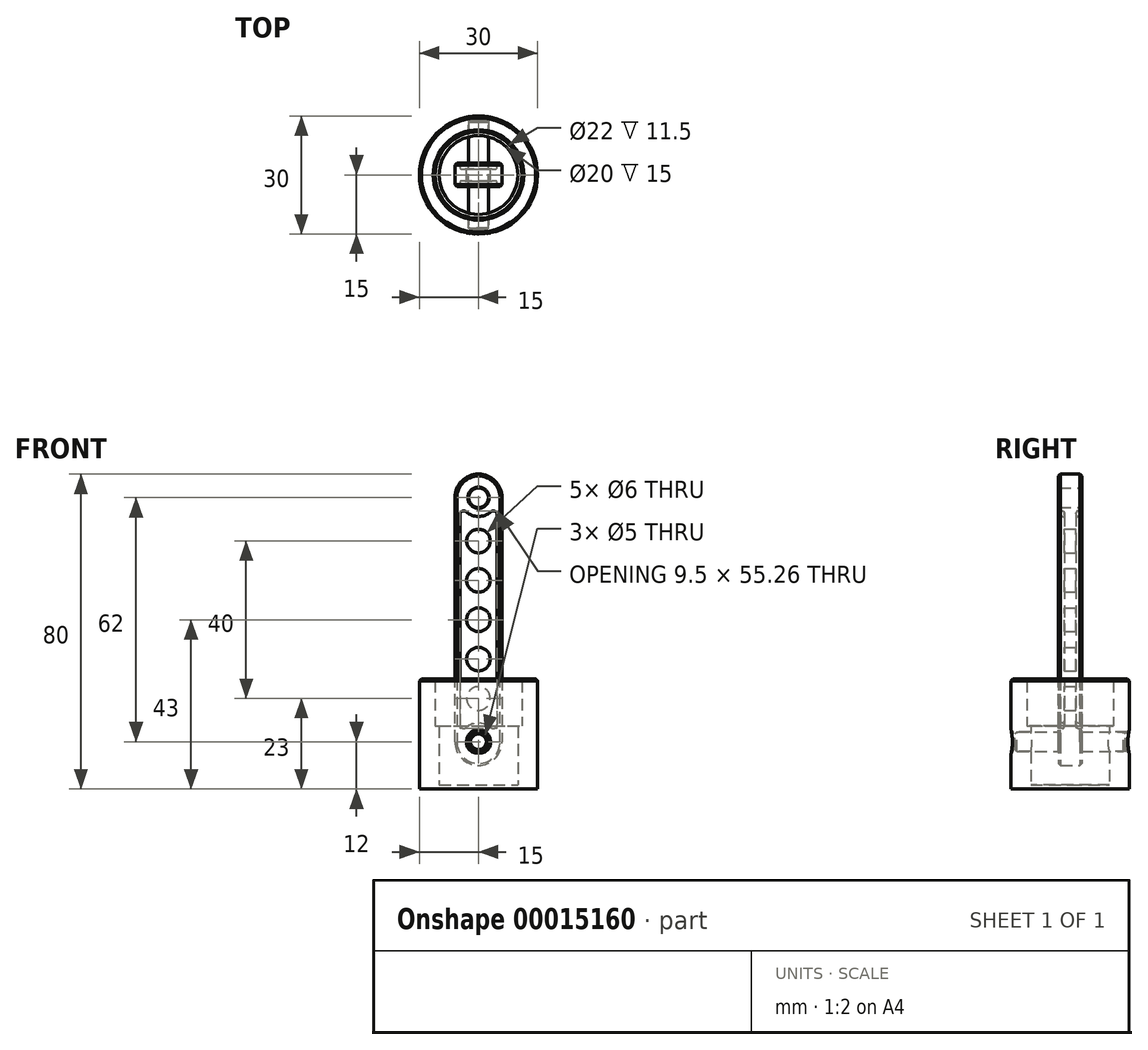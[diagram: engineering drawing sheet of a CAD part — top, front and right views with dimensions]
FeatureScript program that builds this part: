
annotation { "Feature Type Name" : "Feature", "Feature Type Description" : "" }
export const myFeature = defineFeature(function(context is Context, id is Id, definition is map)
    precondition{}
    {
        {
            var Q0;
            Q0=qCreatedBy(makeId("Front.planeOp"),FACE);
            var sketch = newSketch(context, id + "F0", { "sketchPlane" : qUnion([Q0])});
            skLineSegment(sketch, "E0", {"start": v(0, 0) * mm, "end": v(15, 0) * mm});
            skLineSegment(sketch, "E1", {"start": v(15, 0) * mm, "end": v(15, 28) * mm});
            skLineSegment(sketch, "E2", {"start": v(15, 28) * mm, "end": v(11, 28) * mm});
            skLineSegment(sketch, "E3", {"start": v(11, 28) * mm, "end": v(11, 16) * mm});
            skLineSegment(sketch, "E4", {"start": v(11, 16) * mm, "end": v(10, 16) * mm});
            skLineSegment(sketch, "E5", {"start": v(10, 16) * mm, "end": v(10, 1) * mm});
            skLineSegment(sketch, "E6", {"start": v(10, 1) * mm, "end": v(0, 1) * mm});
            skLineSegment(sketch, "E7", {"start": v(0, 1) * mm, "end": v(0, 0) * mm});
            skLineSegment(sketch, "E8", {"start": v(0, 0) * mm, "end": v(0, 33.28) * mm, "construction": true});
            skCircle(sketch, "E9", {"center": v(0, 12) * mm, "radius": 2.5 * mm});
            skSolve(sketch);
        }
        {
            var Q0;
            Q0=makeQuery(id+"F0.imprint","IMPRINT",FACE,{"disambiguationData":[TD([[makeQuery(id+"F0.imprint","IMPRINT",EDGE,{"derivedFrom":sQuery(id+"F0.wireOp",EDGE,"E0")}),1.0]])]});
            var Q1;
            Q1=sQuery(id+"F0.wireOp",EDGE,"E8");
            revolve(context, id + "F1", {"entities" : qUnion([Q0]), "axis" : qUnion([Q1]), "revolveType" : RevolveType.FULL});
        }
        {
            var Q0;
            Q0=makeQuery(id+"F0.imprint","IMPRINT",FACE,{"disambiguationData":[TD([[makeQuery(id+"F0.imprint","IMPRINT",EDGE,{"derivedFrom":sQuery(id+"F0.wireOp",EDGE,"E9")}),1.0]])]});
            extrude(context, id + "F2", {"entities" : qUnion([Q0]), "operationType" : NewBodyOperationType.REMOVE, "endBound" : BoundingType.THROUGH_ALL, "oppositeDirection" : true, "depth" : 44.36 * mm, "hasSecondDirection" : true, "secondDirectionBound" : SecondDirectionBoundingType.THROUGH_ALL, "secondDirectionOppositeDirection" : false, "secondDirectionDepth" : 25 * mm});
        }
        {
            var Q0;
            Q0=makeQuery(id+"F1.opRevolve","SWEPT_EDGE",EDGE,{"disambiguationData":[OSD([sQuery(id+"F0.wireOp",EDGE,"E1"),sQuery(id+"F0.wireOp",EDGE,"E2")])]});
            var Q1;
            Q1=makeQuery(id+"F1.opRevolve","SWEPT_EDGE",EDGE,{"disambiguationData":[OSD([sQuery(id+"F0.wireOp",EDGE,"E2"),sQuery(id+"F0.wireOp",EDGE,"E3")])]});
            chamfer(context, id + "F3", {"entities" : qUnion([Q0, Q1]), "width" : .5 * mm, "tangentPropagation" : true});
        }
        {
            var Q0;
            Q0=makeQuery(id+"F2.boolean.opBoolean","INTERSECT",EDGE,{"disambiguationData":[OD(0.0)],"derivedFrom":[makeQuery(id+"F1.opRevolve","SWEPT_FACE",FACE,{"disambiguationData":[OSD([sQuery(id+"F0.wireOp",EDGE,"E1")])]}),makeQuery(id+"F2.opExtrude","SWEPT_FACE",FACE,{"disambiguationData":[OSD([sQuery(id+"F0.wireOp",EDGE,"E9")])]})]});
            var Q1;
            Q1=makeQuery(id+"F2.boolean.opBoolean","INTERSECT",EDGE,{"disambiguationData":[OD(1.0)],"derivedFrom":[makeQuery(id+"F1.opRevolve","SWEPT_FACE",FACE,{"disambiguationData":[OSD([sQuery(id+"F0.wireOp",EDGE,"E1")])]}),makeQuery(id+"F2.opExtrude","SWEPT_FACE",FACE,{"disambiguationData":[OSD([sQuery(id+"F0.wireOp",EDGE,"E9")])]})]});
            chamfer(context, id + "F4", {"entities" : qUnion([Q0, Q1]), "width" : .5 * mm, "tangentPropagation" : true});
        }
        {
            var Q0;
            Q0=makeQuery(id+"F0.imprint","IMPRINT",FACE,{"disambiguationData":[TD([[makeQuery(id+"F0.imprint","IMPRINT",EDGE,{"derivedFrom":sQuery(id+"F0.wireOp",EDGE,"E9")}),1.0]])]});
            var Q1;
            Q1=sQuery(id+"F0.wireOp",EDGE,"E9");
            extrude(context, id + "F5", {"entities" : qUnion([Q0]), "surfaceEntities" : qUnion([Q1]), "endBound" : BoundingType.SYMMETRIC, "depth" : 28 * mm});
        }
        {
            var Q0;
            Q0=makeQuery(id+"F5.opExtrude","CAP_EDGE",EDGE,{"disambiguationData":[OSD([sQuery(id+"F0.wireOp",EDGE,"E9")])],"isStart":true});
            var Q1;
            Q1=makeQuery(id+"F5.opExtrude","CAP_EDGE",EDGE,{"disambiguationData":[OSD([sQuery(id+"F0.wireOp",EDGE,"E9")])],"isStart":false});
            chamfer(context, id + "F6", {"entities" : qUnion([Q0, Q1]), "width" : .5 * mm, "tangentPropagation" : true});
        }
        {
            var Q0;
            Q0=qCreatedBy(makeId("Front.planeOp"),FACE);
            var sketch = newSketch(context, id + "F7", { "sketchPlane" : qUnion([Q0])});
            skCircle(sketch, "E10.0", {"center": v(0, 12) * mm, "radius": 2.5 * mm});
            skLineSegment(sketch, "E11", {"start": v(0, 12) * mm, "end": v(0, 74) * mm, "construction": true});
            skCircle(sketch, "E12", {"center": v(0, 74) * mm, "radius": 2.5 * mm});
            skLineSegment(sketch, "E13", {"start": v(-6, 74) * mm, "end": v(-6, 12) * mm});
            skLineSegment(sketch, "E14", {"start": v(6, 74) * mm, "end": v(6, 12) * mm});
            skArc(sketch, "E15.converted", {"start": v(6, 74) * mm, "mid": v(0, 80) * mm, "end": v(-6, 74) * mm});
            skArc(sketch, "E16.converted", {"start": v(-6, 12) * mm, "mid": v(0, 6) * mm, "end": v(6, 12) * mm});
            skLineSegment(sketch, "E17.0", {"start": v(4.75, 69.64) * mm, "end": v(4.75, 16.36) * mm});
            skLineSegment(sketch, "E18.0", {"start": v(-4.75, 69.64) * mm, "end": v(-4.75, 16.36) * mm});
            skArc(sketch, "E19", {"start": v(3.1, 15.6) * mm, "mid": v(0, 16.75) * mm, "end": v(-3.1, 15.6) * mm});
            skArc(sketch, "E20", {"start": v(-3.1, 70.4) * mm, "mid": v(0, 69.25) * mm, "end": v(3.1, 70.4) * mm});
            skPoint(sketch, "E21.visualSharp", {"position": v(-4.75, 74) * mm});
            skArc(sketch, "E21.filletArc", {"start": v(-3.1, 70.4) * mm, "mid": v(-4.17, 70.55) * mm, "end": v(-4.75, 69.64) * mm});
            skPoint(sketch, "E22.visualSharp", {"position": v(4.75, 74) * mm});
            skArc(sketch, "E22.filletArc", {"start": v(4.75, 69.64) * mm, "mid": v(4.17, 70.55) * mm, "end": v(3.1, 70.4) * mm});
            skPoint(sketch, "E23.visualSharp", {"position": v(-4.75, 12) * mm});
            skArc(sketch, "E23.filletArc", {"start": v(-4.75, 16.36) * mm, "mid": v(-4.17, 15.45) * mm, "end": v(-3.1, 15.6) * mm});
            skPoint(sketch, "E24.visualSharp", {"position": v(4.75, 12) * mm});
            skArc(sketch, "E24.filletArc", {"start": v(3.1, 15.6) * mm, "mid": v(4.17, 15.45) * mm, "end": v(4.75, 16.36) * mm});
            skCircle(sketch, "E25", {"center": v(0, 63) * mm, "radius": 3 * mm});
            skCircle(sketch, "E26", {"center": v(0, 53) * mm, "radius": 3 * mm});
            skCircle(sketch, "E27", {"center": v(0, 43) * mm, "radius": 3 * mm});
            skCircle(sketch, "E28", {"center": v(0, 33) * mm, "radius": 3 * mm});
            skCircle(sketch, "E29", {"center": v(0, 23) * mm, "radius": 3 * mm});
            skSolve(sketch);
        }
        {
            var Q0;
            Q0=makeQuery(id+"F7.imprint","IMPRINT",FACE,{"disambiguationData":[TD([[makeQuery(id+"F7.imprint","IMPRINT",EDGE,{"derivedFrom":sQuery(id+"F7.wireOp",EDGE,"E10.0")}),-1.0]])]});
            var Q1;
            Q1=makeQuery(id+"F7.imprint","IMPRINT",FACE,{"disambiguationData":[TD([[makeQuery(id+"F7.imprint","IMPRINT",EDGE,{"derivedFrom":sQuery(id+"F7.wireOp",EDGE,"E17.0")}),-1.0]])]});
            extrude(context, id + "F8", {"entities" : qUnion([Q0, Q1]), "depth" : 6 / 2 * mm});
        }
        {
            var Q0;
            Q0=makeQuery(id+"F8.opExtrude","CAP_FACE",FACE,{"disambiguationData":[OSD([sQuery(id+"F7.wireOp",EDGE,"E10.0"),sQuery(id+"F7.wireOp",EDGE,"E12"),sQuery(id+"F7.wireOp",EDGE,"E13"),sQuery(id+"F7.wireOp",EDGE,"E14"),sQuery(id+"F7.wireOp",EDGE,"E15.converted"),sQuery(id+"F7.wireOp",EDGE,"E16.converted"),sQuery(id+"F7.wireOp",EDGE,"E25"),sQuery(id+"F7.wireOp",EDGE,"E26"),sQuery(id+"F7.wireOp",EDGE,"E27"),sQuery(id+"F7.wireOp",EDGE,"E28"),sQuery(id+"F7.wireOp",EDGE,"E29")])],"isStart":false});
            var sketch = newSketch(context, id + "F9", { "sketchPlane" : qUnion([Q0])});
            skLineSegment(sketch, "E30.0", {"start": v(-4.75, 69.64) * mm, "end": v(-4.75, 16.36) * mm});
            skArc(sketch, "E31.0", {"start": v(-3.1, 70.4) * mm, "mid": v(-4.17, 70.55) * mm, "end": v(-4.75, 69.64) * mm});
            skArc(sketch, "E32.0", {"start": v(-3.1, 70.4) * mm, "mid": v(0, 69.25) * mm, "end": v(3.1, 70.4) * mm});
            skArc(sketch, "E33.0", {"start": v(4.75, 69.64) * mm, "mid": v(4.17, 70.55) * mm, "end": v(3.1, 70.4) * mm});
            skLineSegment(sketch, "E34.0", {"start": v(4.75, 69.64) * mm, "end": v(4.75, 16.36) * mm});
            skArc(sketch, "E35.0.0", {"start": v(6, 74) * mm, "mid": v(0, 80) * mm, "end": v(-6, 74) * mm});
            skLineSegment(sketch, "E35.0.1", {"start": v(-6, 74) * mm, "end": v(-6, 12) * mm});
            skArc(sketch, "E35.0.2", {"start": v(-6, 12) * mm, "mid": v(0, 6) * mm, "end": v(6, 12) * mm});
            skLineSegment(sketch, "E35.0.3", {"start": v(6, 12) * mm, "end": v(6, 74) * mm});
            skArc(sketch, "E36.0", {"start": v(3.1, 15.6) * mm, "mid": v(0, 16.75) * mm, "end": v(-3.1, 15.6) * mm});
            skArc(sketch, "E37.0", {"start": v(3.1, 15.6) * mm, "mid": v(4.17, 15.45) * mm, "end": v(4.75, 16.36) * mm});
            skArc(sketch, "E38.0", {"start": v(-4.75, 16.36) * mm, "mid": v(-4.17, 15.45) * mm, "end": v(-3.1, 15.6) * mm});
            skCircle(sketch, "E39.0.0", {"center": v(0, 23) * mm, "radius": 3 * mm});
            skCircle(sketch, "E40.0", {"center": v(0, 33) * mm, "radius": 3 * mm});
            skCircle(sketch, "E41.0", {"center": v(0, 43) * mm, "radius": 3 * mm});
            skCircle(sketch, "E42.0", {"center": v(0, 53) * mm, "radius": 3 * mm});
            skCircle(sketch, "E43.0", {"center": v(0, 63) * mm, "radius": 3 * mm});
            skSolve(sketch);
        }
        {
            var Q0;
            Q0=makeQuery(id+"F9.imprint","IMPRINT",FACE,{"disambiguationData":[TD([[makeQuery(id+"F9.imprint","IMPRINT",EDGE,{"derivedFrom":sQuery(id+"F9.wireOp",EDGE,"E30.0")}),1.0]])]});
            extrude(context, id + "F10", {"entities" : qUnion([Q0]), "operationType" : NewBodyOperationType.REMOVE, "oppositeDirection" : true, "depth" : 1.5 * mm});
        }
        {
            var Q0;
            Q0=makeQuery(id+"F8.opExtrude","CAP_EDGE",EDGE,{"disambiguationData":[OSD([sQuery(id+"F7.wireOp",EDGE,"E14")])],"isStart":false});
            chamfer(context, id + "F11", {"entities" : qUnion([Q0]), "width" : .5 * mm, "tangentPropagation" : true});
        }
        {
            var Q0;
            Q0=makeQuery(id+"F10.boolean.opBoolean","COPY",EDGE,{"derivedFrom":makeQuery(id+"F10.opExtrude","CAP_EDGE",EDGE,{"disambiguationData":[OSD([sQuery(id+"F9.wireOp",EDGE,"E34.0")])],"isStart":false})});
            var Q1;
            Q1=makeQuery(id+"F10.boolean.opBoolean","COPY",EDGE,{"derivedFrom":makeQuery(id+"F10.opExtrude","CAP_EDGE",EDGE,{"disambiguationData":[OSD([sQuery(id+"F9.wireOp",EDGE,"E30.0")])],"isStart":true})});
            fillet(context, id + "F12", {"entities" : qUnion([Q0, Q1]), "radius" : .5 * mm, "tangentPropagation" : true, "allowEdgeOverflow" : false});
        }
        {
            var Q0;
            Q0=makeQuery(id+"F8.opExtrude","CAP_EDGE",EDGE,{"disambiguationData":[OSD([sQuery(id+"F7.wireOp",EDGE,"E12")])],"isStart":false});
            var Q1;
            Q1=makeQuery(id+"F8.opExtrude","CAP_EDGE",EDGE,{"disambiguationData":[OSD([sQuery(id+"F7.wireOp",EDGE,"E10.0")])],"isStart":false});
            chamfer(context, id + "F13", {"entities" : qUnion([Q0, Q1]), "width" : .2 * mm, "tangentPropagation" : true});
        }
        {
            var Q0;
            Q0=makeQuery(id+"F8.opExtrude","SWEPT_BODY",BODY,{"disambiguationData":[OSD([sQuery(id+"F7.wireOp",EDGE,"E10.0"),sQuery(id+"F7.wireOp",EDGE,"E12"),sQuery(id+"F7.wireOp",EDGE,"E13"),sQuery(id+"F7.wireOp",EDGE,"E14"),sQuery(id+"F7.wireOp",EDGE,"E15.converted"),sQuery(id+"F7.wireOp",EDGE,"E16.converted"),sQuery(id+"F7.wireOp",EDGE,"E25"),sQuery(id+"F7.wireOp",EDGE,"E26"),sQuery(id+"F7.wireOp",EDGE,"E27"),sQuery(id+"F7.wireOp",EDGE,"E28"),sQuery(id+"F7.wireOp",EDGE,"E29")])]});
            var Q1;
            Q1=makeQuery(id+"F8.opExtrude","CAP_FACE",FACE,{"disambiguationData":[OSD([sQuery(id+"F7.wireOp",EDGE,"E10.0"),sQuery(id+"F7.wireOp",EDGE,"E12"),sQuery(id+"F7.wireOp",EDGE,"E13"),sQuery(id+"F7.wireOp",EDGE,"E14"),sQuery(id+"F7.wireOp",EDGE,"E15.converted"),sQuery(id+"F7.wireOp",EDGE,"E16.converted"),sQuery(id+"F7.wireOp",EDGE,"E25"),sQuery(id+"F7.wireOp",EDGE,"E26"),sQuery(id+"F7.wireOp",EDGE,"E27"),sQuery(id+"F7.wireOp",EDGE,"E28"),sQuery(id+"F7.wireOp",EDGE,"E29")])],"isStart":true});
            mirror(context, id + "F14", {"operationType" : NewBodyOperationType.ADD, "entities" : qUnion([Q0]), "mirrorPlane" : qUnion([Q1])});
        }
    });
